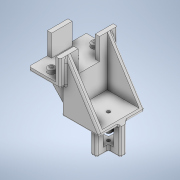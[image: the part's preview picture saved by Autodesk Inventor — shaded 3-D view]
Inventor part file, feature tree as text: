
AUTODESK INVENTOR PART (.ipt)
format: ipt  version: 2020 (Build 240168000, 168)  size: 766,976 bytes
history: native  units: in
note: dims shown in document units (in); Inventor stores cm internally (conversion verified against a paired STEP export)
features: extrude x14, sketch x14, fillet x3, chamfer x2
ambient origin geometry x8: Origin, YZ Plane, XZ Plane, XY Plane, X Axis, Y Axis, Z Axis, Center Point
bodies: Solid1 (feature_tree)
feature tree (33):
  extrude  "Extrusion1"  Depth=2.6378in
  extrude  "Extrusion2"  Depth=0.1969in
  extrude  "Extrusion6"  Depth=0.1969in
  extrude  "Extrusion8"  Depth=1.0in TaperAngle=0.0deg
  chamfer  "Chamfer1"  Distance=1.0in
  extrude  "Extrusion9"  Depth=0.3406in
  extrude  "Extrusion10"  Depth=0.1969in TaperAngle=0.0deg
  extrude  "Extrusion11"  Depth=0.1575in
  extrude  "Extrusion12"  Depth=0.1575in
  extrude  "Extrusion16"  Depth=0.2362in
  extrude  "Extrusion17"  Depth=0.2362in
  extrude  "Extrusion18"  Depth=0.1969in
  extrude  "Extrusion19"  Depth=0.1969in
  extrude  "Extrusion20"  Depth=0.1969in
  chamfer  "Chamfer2"  Distance=1.2992in
  extrude  "Extrusion21"  Depth=0.1969in
  fillet  "Fillet9"  Radius=0.1969in
  fillet  "Fillet10"  Radius=0.1969in
  fillet  "Fillet11"  Radius=1.811in
  sketch  "Sketch1"  dims[d0=1.4331in d1=2.6378in]
  sketch  "Sketch2"  dims[d2=0.1969in d3=0.0in d4=0.1969in]
  sketch  "Sketch6"  dims[d5=0.8268in d6=0.1969in]
  sketch  "Sketch8"  dims[d7=0.8268in d8=1.0in d9=0.0in]
  sketch  "Sketch9"  dims[d26=0.1969in]
  sketch  "Sketch10"  dims[d27=0.9449in d28=1.0in d29=0.0in]
  sketch  "Sketch11"  dims[d37=0.3406in d38=0.3406in]
  sketch  "Sketch12"  dims[d39=0.3406in d40=0.1969in d41=0.0in]
  sketch  "Sketch16"  dims[d42=0.0591in d43=0.0787in d44=45.0deg d45=0.1575in]
  sketch  "Sketch17"  dims[d46=0.1575in d47=0.1575in]
  sketch  "Sketch18"  dims[d48=0.7874in d49=0.0in d50=0.2362in]
  sketch  "Sketch19"  dims[d51=0.2362in d52=0.2362in]
  sketch  "Sketch20"  dims[d53=0.0984in d54=0.0in d55=0.1969in]
  sketch  "Sketch21"  dims[d56=2.0866in d57=0.1969in d58=0.1969in d59=1.2992in d60=0.0in d61=0.1969in d62=0.1969in d63=0.1969in d64=1.811in d65=0.0in d83=0.9055in d84=0.1575in d85=0.3937in d86=0.0in d87=0.3937in d88=0.1575in d89=0.2953in d90=0.2953in d91=0.2953in d92=0.2953in d93=0.2953in d94=0.2953in d95=0.2953in d96=0.2953in d97=0.6299in d98=0.0in d99=0.6102in d100=0.0in d101=0.2953in d102=0.2953in d103=0.2953in d104=0.2953in d105=0.2953in d106=0.0in d107=0.3543in d108=0.6693in d109=0.0in d110=0.0787in d111=0.0787in d112=45.0deg d113=3.937in d114=0.0in d115=0.0787in d116=0.0787in d117=0.0787in d10=0.0197in d11=0.0344in d13=0.0197in d14=0.0344in d15=0.0197in d16=0.0344in d80=0.0197in d81=0.0344in d82=0.0197in]
